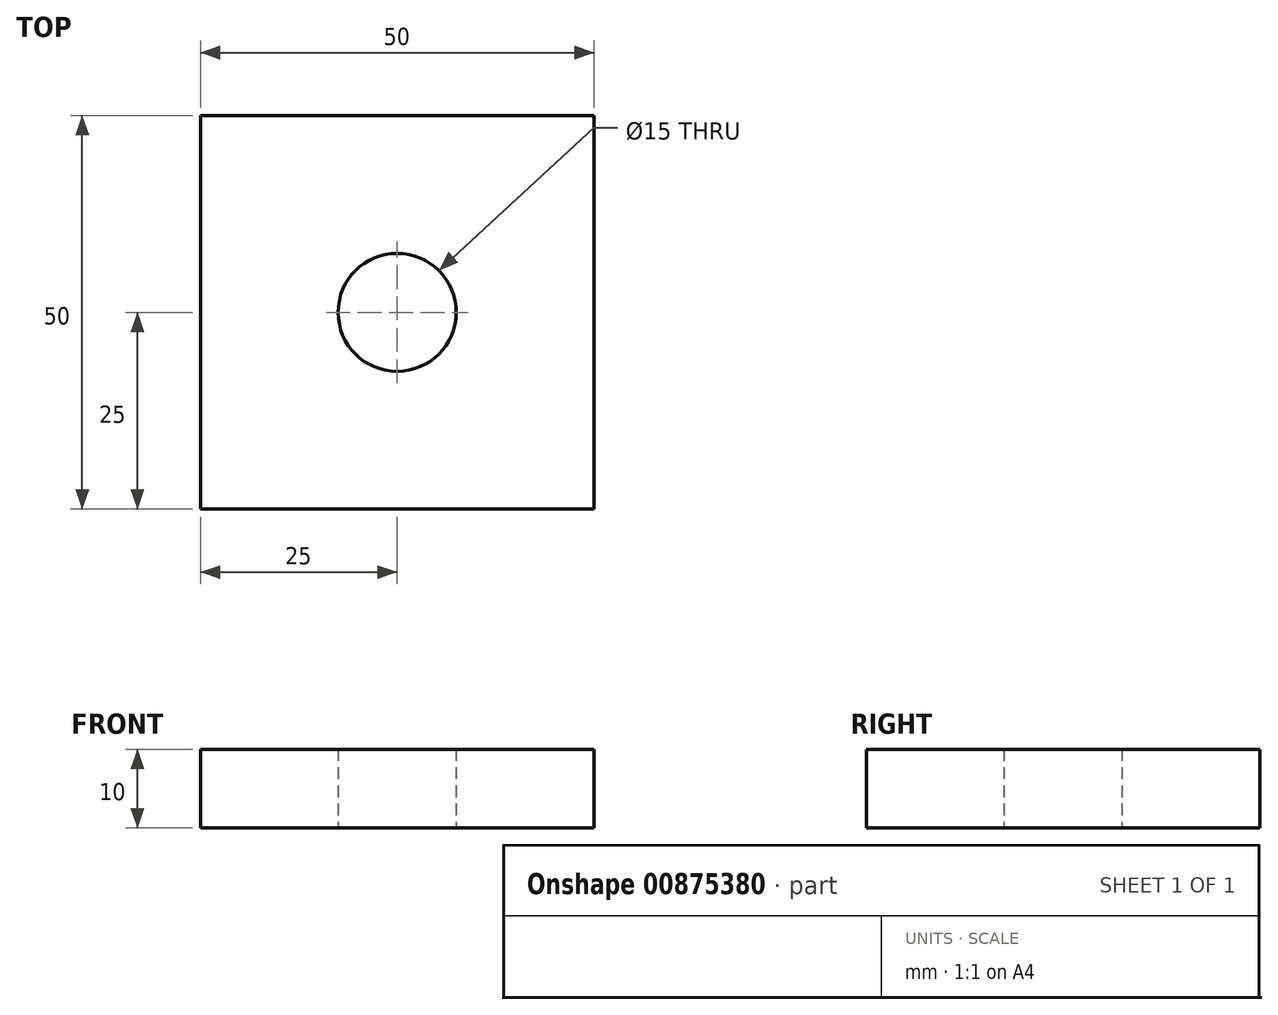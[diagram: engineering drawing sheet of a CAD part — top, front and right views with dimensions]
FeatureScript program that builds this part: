
annotation { "Feature Type Name" : "Feature", "Feature Type Description" : "" }
export const myFeature = defineFeature(function(context is Context, id is Id, definition is map)
    precondition{}
    {
        {
            var Q0;
            Q0=qCreatedBy(makeId("Top.planeOp"),FACE);
            var sketch = newSketch(context, id + "F0", { "sketchPlane" : qUnion([Q0])});
            skLineSegment(sketch, "E0.bottom", {"start": v(25, -25) * mm, "end": v(-25, -25) * mm});
            skLineSegment(sketch, "E0.top", {"start": v(25, 25) * mm, "end": v(-25, 25) * mm});
            skLineSegment(sketch, "E0.left", {"start": v(25, -25) * mm, "end": v(25, 25) * mm});
            skLineSegment(sketch, "E0.right", {"start": v(-25, -25) * mm, "end": v(-25, 25) * mm});
            skPoint(sketch, "E0.middle", {"position": v(0, 0) * mm});
            skCircle(sketch, "E1", {"center": v(0, 0) * mm, "radius": 7.5 * mm});
            skSolve(sketch);
        }
        {
            var Q0;
            Q0=makeQuery(id+"F0.imprint","IMPRINT",FACE,{"disambiguationData":[TD([[makeQuery(id+"F0.imprint","IMPRINT",EDGE,{"derivedFrom":sQuery(id+"F0.wireOp",EDGE,"E0.bottom")}),-1.0]])]});
            extrude(context, id + "F1", {"entities" : qUnion([Q0]), "depth" : 10 * mm, "offsetDistance" : 25 * mm});
        }
    });
